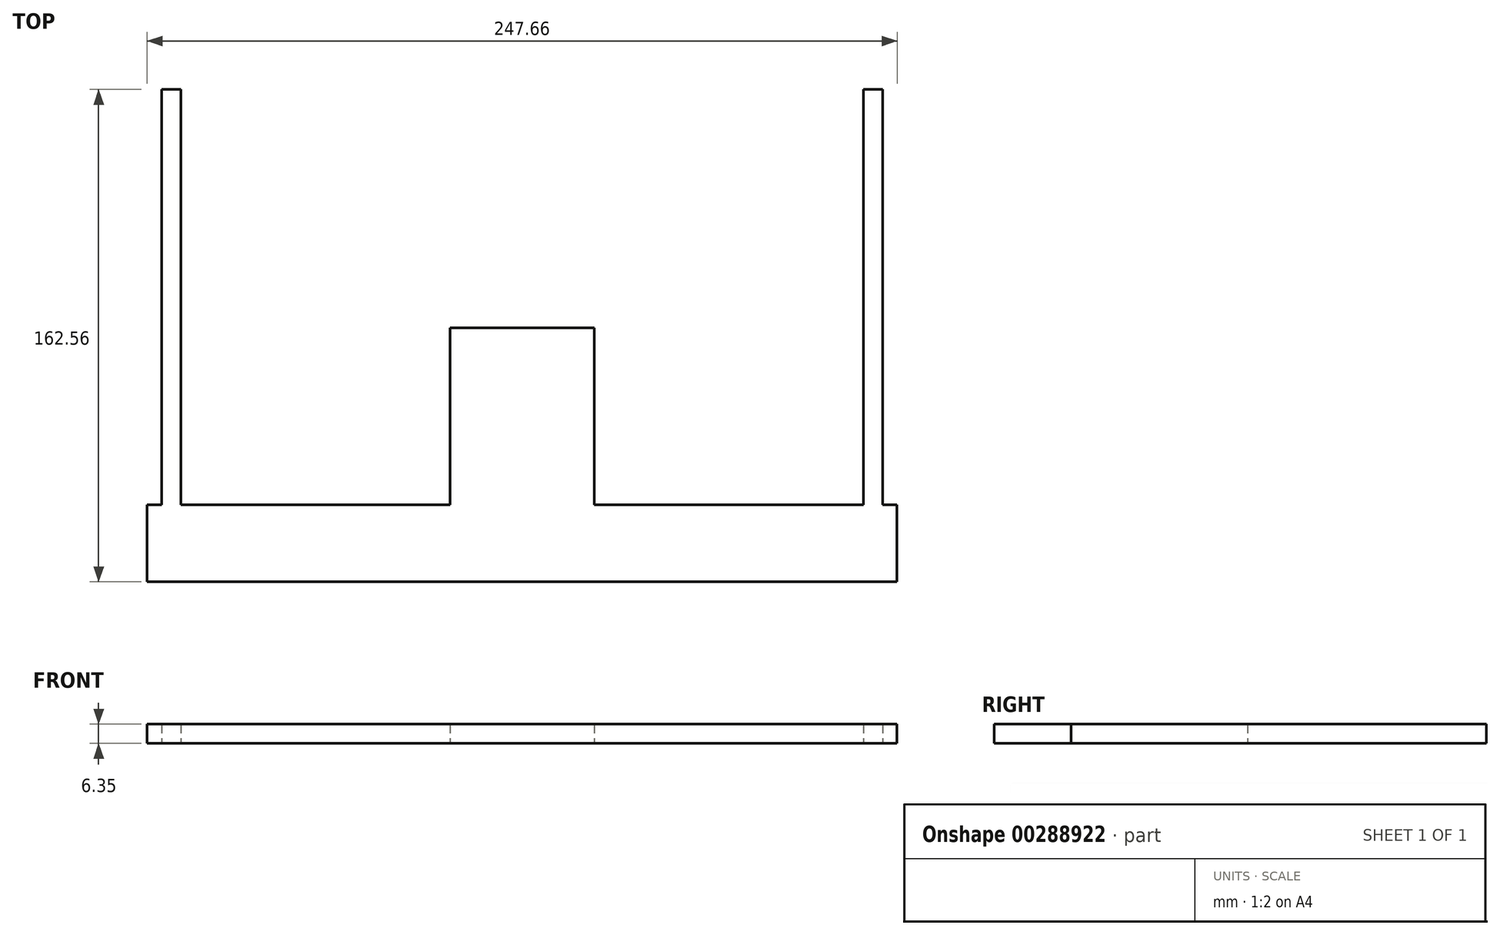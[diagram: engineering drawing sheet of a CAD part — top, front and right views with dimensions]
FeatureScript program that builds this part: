
annotation { "Feature Type Name" : "Feature", "Feature Type Description" : "" }
export const myFeature = defineFeature(function(context is Context, id is Id, definition is map)
    precondition{}
    {
        {
            var Q0;
            Q0=qCreatedBy(makeId("Top.planeOp"),FACE);
            var sketch = newSketch(context, id + "F0", { "sketchPlane" : qUnion([Q0])});
            skLineSegment(sketch, "E0.bottom", {"start": v(-23.81, 41.91) * mm, "end": v(23.81, 41.91) * mm});
            skLineSegment(sketch, "E0.top", {"start": v(-23.81, -41.9) * mm, "end": v(23.81, -41.9) * mm});
            skLineSegment(sketch, "E0.left", {"start": v(-23.81, 41.9) * mm, "end": v(-23.81, -41.91) * mm});
            skLineSegment(sketch, "E0.right", {"start": v(23.81, 41.91) * mm, "end": v(23.81, -41.91) * mm});
            skPoint(sketch, "E0.middle", {"position": v(0, 0) * mm});
            skLineSegment(sketch, "E1.bottom", {"start": v(-23.81, -41.91) * mm, "end": v(-123.83, -41.91) * mm});
            skLineSegment(sketch, "E1.top", {"start": v(-23.81, -16.51) * mm, "end": v(-112.69, -16.51) * mm});
            skLineSegment(sketch, "E1.left", {"start": v(-23.81, -41.91) * mm, "end": v(-23.81, -16.51) * mm});
            skLineSegment(sketch, "E2.bottom", {"start": v(23.81, -41.91) * mm, "end": v(123.83, -41.91) * mm});
            skLineSegment(sketch, "E2.top", {"start": v(23.81, -16.51) * mm, "end": v(112.69, -16.51) * mm});
            skLineSegment(sketch, "E2.left", {"start": v(23.81, -41.91) * mm, "end": v(23.81, -16.51) * mm});
            skLineSegment(sketch, "E3", {"start": v(0, 0) * mm, "end": v(0, 73.84) * mm, "construction": true});
            skLineSegment(sketch, "E4", {"start": v(0, 0) * mm, "end": v(0, -45.07) * mm, "construction": true});
            skLineSegment(sketch, "E5", {"start": v(-119.04, -16.51) * mm, "end": v(-119.04, 120.65) * mm});
            skLineSegment(sketch, "E6", {"start": v(-119.04, 120.65) * mm, "end": v(-112.69, 120.65) * mm});
            skLineSegment(sketch, "E7", {"start": v(-112.69, 120.65) * mm, "end": v(-112.69, -16.51) * mm});
            skLineSegment(sketch, "E8", {"start": v(119.04, -16.51) * mm, "end": v(119.04, 120.65) * mm});
            skLineSegment(sketch, "E9", {"start": v(119.04, 120.65) * mm, "end": v(112.69, 120.65) * mm});
            skLineSegment(sketch, "E10", {"start": v(112.69, 120.65) * mm, "end": v(112.69, -16.51) * mm});
            skPoint(sketch, "E11.start.orphan", {"position": v(-123.83, -16.51) * mm});
            skPoint(sketch, "E12.start.orphan", {"position": v(123.83, -16.51) * mm});
            skPoint(sketch, "E13.center.orphan", {"position": v(-123.83, -29.21) * mm});
            skPoint(sketch, "E14.center.orphan", {"position": v(123.83, -29.21) * mm});
            skLineSegment(sketch, "E15", {"start": v(-123.83, -41.91) * mm, "end": v(-123.83, -16.51) * mm});
            skLineSegment(sketch, "E16", {"start": v(123.83, -41.91) * mm, "end": v(123.83, -16.51) * mm});
            skLineSegment(sketch, "E17", {"start": v(119.04, -16.51) * mm, "end": v(123.83, -16.51) * mm});
            skLineSegment(sketch, "E18", {"start": v(-123.83, -16.51) * mm, "end": v(-119.04, -16.51) * mm});
            skSolve(sketch);
        }
        {
            var Q0;
            Q0 = qSketchRegion(id + "F0", true);
            extrude(context, id + "F1", {"entities" : qUnion([Q0]), "depth" : 6.35 * mm});
        }
    });
